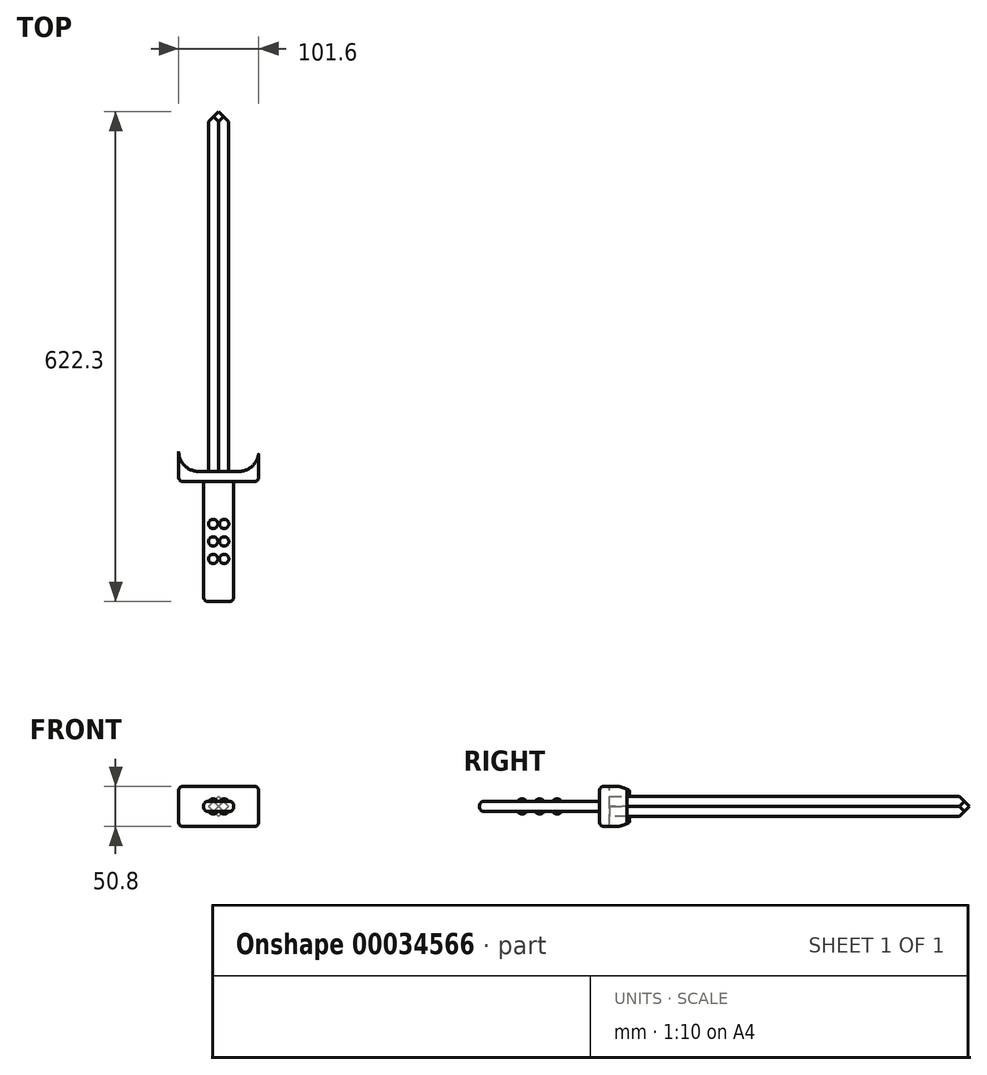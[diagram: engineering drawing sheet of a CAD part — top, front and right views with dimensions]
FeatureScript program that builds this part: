
annotation { "Feature Type Name" : "Feature", "Feature Type Description" : "" }
export const myFeature = defineFeature(function(context is Context, id is Id, definition is map)
    precondition{}
    {
        {
            var Q0;
            Q0=qCreatedBy(makeId("Front.planeOp"),FACE);
            var sketch = newSketch(context, id + "F0", { "sketchPlane" : qUnion([Q0])});
            skLineSegment(sketch, "E0.bottom", {"start": v(-20.15, -10.38) * mm, "end": v(17.95, -10.38) * mm});
            skLineSegment(sketch, "E0.top", {"start": v(-20.15, -23.08) * mm, "end": v(17.95, -23.08) * mm});
            skLineSegment(sketch, "E0.left", {"start": v(-20.15, -10.38) * mm, "end": v(-20.15, -23.08) * mm});
            skLineSegment(sketch, "E0.right", {"start": v(17.95, -10.38) * mm, "end": v(17.95, -23.08) * mm});
            skSolve(sketch);
        }
        {
            var Q0;
            Q0=makeQuery(id+"F0.imprint","IMPRINT",FACE,{"disambiguationData":[TD([[makeQuery(id+"F0.imprint","IMPRINT",EDGE,{"derivedFrom":sQuery(id+"F0.wireOp",EDGE,"E0.bottom")}),-1.0]])]});
            extrude(context, id + "F1", {"entities" : qUnion([Q0]), "oppositeDirection" : true, "depth" : 152.4 * mm});
        }
        {
            var Q0;
            Q0=makeQuery(id+"F1.opExtrude","CAP_FACE",FACE,{"disambiguationData":[OSD([sQuery(id+"F0.wireOp",EDGE,"E0.bottom"),sQuery(id+"F0.wireOp",EDGE,"E0.top"),sQuery(id+"F0.wireOp",EDGE,"E0.left"),sQuery(id+"F0.wireOp",EDGE,"E0.right")])],"isStart":false});
            var sketch = newSketch(context, id + "F2", { "sketchPlane" : qUnion([Q0])});
            skLineSegment(sketch, "E1.bottom", {"start": v(-49.7, 8.67) * mm, "end": v(51.9, 8.67) * mm});
            skLineSegment(sketch, "E1.top", {"start": v(-49.7, -42.13) * mm, "end": v(51.9, -42.13) * mm});
            skLineSegment(sketch, "E1.left", {"start": v(-49.7, 8.67) * mm, "end": v(-49.7, -42.13) * mm});
            skLineSegment(sketch, "E1.right", {"start": v(51.9, 8.67) * mm, "end": v(51.9, -42.13) * mm});
            skSolve(sketch);
        }
        {
            var Q0;
            Q0=makeQuery(id+"F2.imprint","IMPRINT",FACE,{"disambiguationData":[TD([[makeQuery(id+"F2.imprint","IMPRINT",EDGE,{"derivedFrom":sQuery(id+"F2.wireOp",EDGE,"E1.bottom")}),-1.0]])]});
            var Q1;
            Q1=makeQuery(id+"F2.imprint","IMPRINT",FACE,{"disambiguationData":[TD([[makeQuery(id+"F2.imprint","IMPRINT",EDGE,{"derivedFrom":makeQuery(id+"F1.opExtrude","CAP_EDGE",EDGE,{"disambiguationData":[OSD([sQuery(id+"F0.wireOp",EDGE,"E0.bottom")])],"isStart":false})}),1.0]])]});
            extrude(context, id + "F3", {"entities" : qUnion([Q0, Q1]), "operationType" : NewBodyOperationType.ADD, "depth" : 12.7 * mm});
        }
        {
            var Q0;
            Q0=makeQuery(id+"F3.opExtrude","CAP_EDGE",EDGE,{"disambiguationData":[OSD([sQuery(id+"F2.wireOp",EDGE,"E1.bottom")])],"isStart":true});
            var Q1;
            Q1=makeQuery(id+"F1.opExtrude","CAP_EDGE",EDGE,{"disambiguationData":[OSD([sQuery(id+"F0.wireOp",EDGE,"E0.right")])],"isStart":false});
            var Q2;
            Q2=makeQuery(id+"F1.opExtrude","CAP_EDGE",EDGE,{"disambiguationData":[OSD([sQuery(id+"F0.wireOp",EDGE,"E0.bottom")])],"isStart":false});
            var Q3;
            Q3=makeQuery(id+"F1.opExtrude","CAP_EDGE",EDGE,{"disambiguationData":[OSD([sQuery(id+"F0.wireOp",EDGE,"E0.left")])],"isStart":false});
            var Q4;
            Q4=makeQuery(id+"F1.opExtrude","CAP_EDGE",EDGE,{"disambiguationData":[OSD([sQuery(id+"F0.wireOp",EDGE,"E0.top")])],"isStart":false});
            var Q5;
            Q5=makeQuery(id+"F3.opExtrude","CAP_EDGE",EDGE,{"disambiguationData":[OSD([sQuery(id+"F2.wireOp",EDGE,"E1.left")])],"isStart":true});
            var Q6;
            Q6=makeQuery(id+"F3.opExtrude","CAP_EDGE",EDGE,{"disambiguationData":[OSD([sQuery(id+"F2.wireOp",EDGE,"E1.top")])],"isStart":true});
            var Q7;
            Q7=makeQuery(id+"F3.opExtrude","CAP_EDGE",EDGE,{"disambiguationData":[OSD([sQuery(id+"F2.wireOp",EDGE,"E1.right")])],"isStart":true});
            var Q8;
            Q8=makeQuery(id+"F1.opExtrude","SWEPT_EDGE",EDGE,{"disambiguationData":[OSD([sQuery(id+"F0.wireOp",EDGE,"E0.bottom"),sQuery(id+"F0.wireOp",EDGE,"E0.right")])]});
            var Q9;
            Q9=makeQuery(id+"F1.opExtrude","SWEPT_EDGE",EDGE,{"disambiguationData":[OSD([sQuery(id+"F0.wireOp",EDGE,"E0.top"),sQuery(id+"F0.wireOp",EDGE,"E0.right")])]});
            var Q10;
            Q10=makeQuery(id+"F1.opExtrude","CAP_EDGE",EDGE,{"disambiguationData":[OSD([sQuery(id+"F0.wireOp",EDGE,"E0.top")])],"isStart":true});
            var Q11;
            Q11=makeQuery(id+"F1.opExtrude","CAP_EDGE",EDGE,{"disambiguationData":[OSD([sQuery(id+"F0.wireOp",EDGE,"E0.bottom")])],"isStart":true});
            var Q12;
            Q12=makeQuery(id+"F1.opExtrude","SWEPT_EDGE",EDGE,{"disambiguationData":[OSD([sQuery(id+"F0.wireOp",EDGE,"E0.bottom"),sQuery(id+"F0.wireOp",EDGE,"E0.left")])]});
            var Q13;
            Q13=makeQuery(id+"F1.opExtrude","SWEPT_EDGE",EDGE,{"disambiguationData":[OSD([sQuery(id+"F0.wireOp",EDGE,"E0.top"),sQuery(id+"F0.wireOp",EDGE,"E0.left")])]});
            var Q14;
            Q14=makeQuery(id+"F1.opExtrude","CAP_EDGE",EDGE,{"disambiguationData":[OSD([sQuery(id+"F0.wireOp",EDGE,"E0.left")])],"isStart":true});
            var Q15;
            Q15=makeQuery(id+"F1.opExtrude","CAP_EDGE",EDGE,{"disambiguationData":[OSD([sQuery(id+"F0.wireOp",EDGE,"E0.right")])],"isStart":true});
            fillet(context, id + "F4", {"entities" : qUnion([Q0, Q1, Q2, Q3, Q4, Q5, Q6, Q7, Q8, Q9, Q10, Q11, Q12, Q13, Q14, Q15]), "radius" : 5.08 * mm, "tangentPropagation" : true, "allowEdgeOverflow" : false});
        }
        {
            var Q0;
            Q0=makeQuery(id+"F3.opExtrude","SWEPT_FACE",FACE,{"disambiguationData":[OSD([sQuery(id+"F2.wireOp",EDGE,"E1.bottom")])]});
            var sketch = newSketch(context, id + "F5", { "sketchPlane" : qUnion([Q0])});
            skLineSegment(sketch, "E2.bottom", {"start": v(-51.9, 165.1) * mm, "end": v(49.7, 165.1) * mm});
            skLineSegment(sketch, "E2.left", {"start": v(-51.9, 165.1) * mm, "end": v(-51.9, 190.5) * mm});
            skLineSegment(sketch, "E2.right", {"start": v(49.7, 165.1) * mm, "end": v(49.7, 190.5) * mm});
            skLineSegment(sketch, "E3.bottom", {"start": v(-51.9, 165.1) * mm, "end": v(-26.5, 165.1) * mm});
            skLineSegment(sketch, "E4.bottom", {"start": v(49.7, 165.1) * mm, "end": v(24.3, 165.1) * mm});
            skArc(sketch, "E5", {"start": v(-51.9, 190.5) * mm, "mid": v(-44.46, 172.54) * mm, "end": v(-26.5, 165.1) * mm});
            skArc(sketch, "E6", {"start": v(24.3, 165.1) * mm, "mid": v(42.26, 172.54) * mm, "end": v(49.7, 190.5) * mm});
            skSolve(sketch);
        }
        {
            var Q0;
            Q0 = qSketchRegion(id + "F5", true);
            extrude(context, id + "F6", {"entities" : qUnion([Q0]), "operationType" : NewBodyOperationType.ADD, "oppositeDirection" : true, "depth" : 50.8 * mm});
        }
        {
            var Q0;
            Q0=makeQuery(id+"F6.boolean.opBoolean","MERGE",EDGE,{"derivedFrom":[makeQuery(id+"F3.opExtrude","SWEPT_EDGE",EDGE,{"disambiguationData":[OSD([sQuery(id+"F2.wireOp",EDGE,"E1.bottom"),sQuery(id+"F2.wireOp",EDGE,"E1.left")])]}),makeQuery(id+"F6.opExtrude","CAP_EDGE",EDGE,{"disambiguationData":[OSD([sQuery(id+"F5.wireOp",EDGE,"92b06a6b-4f89-4f7e-b0d3-59be5738ee68.left")])],"isStart":true})]});
            var Q1;
            Q1=makeQuery(id+"F6.opExtrude","CAP_EDGE",EDGE,{"disambiguationData":[OSD([sQuery(id+"F5.wireOp",EDGE,"0fc54be1-5544-46dc-9fd6-cf08e8844ddd")])],"isStart":true});
            var Q2;
            Q2=makeQuery(id+"F6.opExtrude","CAP_EDGE",EDGE,{"disambiguationData":[OSD([sQuery(id+"F5.wireOp",EDGE,"522da2e3-5dac-4369-9592-a29fee154710.trimOffspring")])],"isStart":false});
            var Q3;
            Q3=makeQuery(id+"F6.boolean.opBoolean","MERGE",EDGE,{"derivedFrom":[makeQuery(id+"F3.opExtrude","SWEPT_EDGE",EDGE,{"disambiguationData":[OSD([sQuery(id+"F2.wireOp",EDGE,"E1.top"),sQuery(id+"F2.wireOp",EDGE,"E1.left")])]}),makeQuery(id+"F6.opExtrude","CAP_EDGE",EDGE,{"disambiguationData":[OSD([sQuery(id+"F5.wireOp",EDGE,"92b06a6b-4f89-4f7e-b0d3-59be5738ee68.left")])],"isStart":false})]});
            var Q4;
            Q4=makeQuery(id+"F6.boolean.opBoolean","MERGE",EDGE,{"derivedFrom":[makeQuery(id+"F3.opExtrude","SWEPT_EDGE",EDGE,{"disambiguationData":[OSD([sQuery(id+"F2.wireOp",EDGE,"E1.bottom"),sQuery(id+"F2.wireOp",EDGE,"E1.right")])]}),makeQuery(id+"F6.opExtrude","CAP_EDGE",EDGE,{"disambiguationData":[OSD([sQuery(id+"F5.wireOp",EDGE,"92b06a6b-4f89-4f7e-b0d3-59be5738ee68.right")])],"isStart":true})]});
            var Q5;
            Q5=makeQuery(id+"F6.boolean.opBoolean","MERGE",EDGE,{"derivedFrom":[makeQuery(id+"F3.opExtrude","SWEPT_EDGE",EDGE,{"disambiguationData":[OSD([sQuery(id+"F2.wireOp",EDGE,"E1.top"),sQuery(id+"F2.wireOp",EDGE,"E1.right")])]}),makeQuery(id+"F6.opExtrude","CAP_EDGE",EDGE,{"disambiguationData":[OSD([sQuery(id+"F5.wireOp",EDGE,"92b06a6b-4f89-4f7e-b0d3-59be5738ee68.right")])],"isStart":false})]});
            fillet(context, id + "F7", {"entities" : qUnion([Q0, Q1, Q2, Q3, Q4, Q5]), "radius" : 5.08 * mm, "tangentPropagation" : true, "allowEdgeOverflow" : false});
        }
        {
            var Q0;
            Q0=makeQuery(id+"F3.opExtrude","CAP_FACE",FACE,{"disambiguationData":[OSD([sQuery(id+"F2.wireOp",EDGE,"E1.bottom"),sQuery(id+"F2.wireOp",EDGE,"E1.top"),sQuery(id+"F2.wireOp",EDGE,"E1.left"),sQuery(id+"F2.wireOp",EDGE,"E1.right")])],"isStart":false});
            var sketch = newSketch(context, id + "F8", { "sketchPlane" : qUnion([Q0])});
            skLineSegment(sketch, "E7.bottom", {"start": v(-11.6, -4.03) * mm, "end": v(13.8, -4.03) * mm});
            skLineSegment(sketch, "E7.top", {"start": v(-11.6, -29.43) * mm, "end": v(13.8, -29.43) * mm});
            skLineSegment(sketch, "E7.left", {"start": v(-11.6, -4.03) * mm, "end": v(-11.6, -29.43) * mm});
            skLineSegment(sketch, "E7.right", {"start": v(13.8, -4.03) * mm, "end": v(13.8, -29.43) * mm});
            skSolve(sketch);
        }
        {
            var Q0;
            Q0 = qSketchRegion(id + "F8", true);
            extrude(context, id + "F9", {"entities" : qUnion([Q0]), "operationType" : NewBodyOperationType.ADD, "depth" : 457.2 * mm});
        }
        {
            var Q0;
            Q0=makeQuery(id+"F6.opExtrude","SWEPT_EDGE",EDGE,{"disambiguationData":[OSD([sQuery(id+"F5.wireOp",EDGE,"E2.right"),sQuery(id+"F5.wireOp",EDGE,"E6")])]});
            fillet(context, id + "F10", {"entities" : qUnion([Q0]), "radius" : 0.13 * mm, "tangentPropagation" : true, "allowEdgeOverflow" : false});
        }
        {
            var Q0;
            Q0=makeQuery(id+"F9.opExtrude","CAP_EDGE",EDGE,{"disambiguationData":[OSD([sQuery(id+"F8.wireOp",EDGE,"E7.bottom")])],"isStart":false});
            var Q1;
            Q1=makeQuery(id+"F9.opExtrude","CAP_EDGE",EDGE,{"disambiguationData":[OSD([sQuery(id+"F8.wireOp",EDGE,"E7.top")])],"isStart":false});
            var Q2;
            Q2=makeQuery(id+"F9.opExtrude","CAP_EDGE",EDGE,{"disambiguationData":[OSD([sQuery(id+"F8.wireOp",EDGE,"E7.left")])],"isStart":false});
            var Q3;
            Q3=makeQuery(id+"F9.opExtrude","CAP_EDGE",EDGE,{"disambiguationData":[OSD([sQuery(id+"F8.wireOp",EDGE,"E7.right")])],"isStart":false});
            chamfer(context, id + "F11", {"entities" : qUnion([Q0, Q1, Q2, Q3]), "width" : 12.7 * mm, "tangentPropagation" : true});
        }
        {
            var Q0;
            Q0=makeQuery(id+"F9.opExtrude","SWEPT_EDGE",EDGE,{"disambiguationData":[OSD([sQuery(id+"F5.wireOp",EDGE,"92b06a6b-4f89-4f7e-b0d3-59be5738ee68.bottom"),sQuery(id+"F5.wireOp",EDGE,"0fc54be1-5544-46dc-9fd6-cf08e8844ddd"),sQuery(id+"F8.wireOp",EDGE,"E7.top"),sQuery(id+"F8.wireOp",EDGE,"E7.left")])]});
            var Q1;
            Q1=makeQuery(id+"F9.opExtrude","SWEPT_EDGE",EDGE,{"disambiguationData":[OSD([sQuery(id+"F5.wireOp",EDGE,"92b06a6b-4f89-4f7e-b0d3-59be5738ee68.bottom"),sQuery(id+"F5.wireOp",EDGE,"522da2e3-5dac-4369-9592-a29fee154710.trimOffspring"),sQuery(id+"F8.wireOp",EDGE,"E7.top"),sQuery(id+"F8.wireOp",EDGE,"E7.right")])]});
            var Q2;
            Q2=makeQuery(id+"F9.opExtrude","SWEPT_EDGE",EDGE,{"disambiguationData":[OSD([sQuery(id+"F5.wireOp",EDGE,"92b06a6b-4f89-4f7e-b0d3-59be5738ee68.bottom"),sQuery(id+"F5.wireOp",EDGE,"0fc54be1-5544-46dc-9fd6-cf08e8844ddd"),sQuery(id+"F8.wireOp",EDGE,"E7.bottom"),sQuery(id+"F8.wireOp",EDGE,"E7.left")])]});
            var Q3;
            Q3=makeQuery(id+"F9.opExtrude","SWEPT_EDGE",EDGE,{"disambiguationData":[OSD([sQuery(id+"F5.wireOp",EDGE,"92b06a6b-4f89-4f7e-b0d3-59be5738ee68.bottom"),sQuery(id+"F5.wireOp",EDGE,"522da2e3-5dac-4369-9592-a29fee154710.trimOffspring"),sQuery(id+"F8.wireOp",EDGE,"E7.bottom"),sQuery(id+"F8.wireOp",EDGE,"E7.right")])]});
            chamfer(context, id + "F12", {"entities" : qUnion([Q0, Q1, Q2, Q3]), "width" : 12.7 * mm, "tangentPropagation" : true});
        }
        {
            var Q0;
            Q0=makeQuery(id+"F1.opExtrude","SWEPT_FACE",FACE,{"disambiguationData":[OSD([sQuery(id+"F0.wireOp",EDGE,"E0.bottom")])]});
            var sketch = newSketch(context, id + "F13", { "sketchPlane" : qUnion([Q0])});
            skCircle(sketch, "E8", {"center": v(-8.09, 98.43) * mm, "radius": 5.91 * mm});
            skCircle(sketch, "E9", {"center": v(5.88, 98.43) * mm, "radius": 5.91 * mm});
            skCircle(sketch, "E10", {"center": v(-8.09, 76.2) * mm, "radius": 5.91 * mm});
            skCircle(sketch, "E11", {"center": v(5.88, 76.2) * mm, "radius": 5.91 * mm});
            skCircle(sketch, "E12", {"center": v(-8.09, 53.97) * mm, "radius": 5.91 * mm});
            skCircle(sketch, "E13", {"center": v(5.88, 53.97) * mm, "radius": 5.91 * mm});
            skLineSegment(sketch, "E14", {"start": v(-8.09, 98.43) * mm, "end": v(-8.09, 76.2) * mm});
            skLineSegment(sketch, "E15", {"start": v(-8.09, 76.2) * mm, "end": v(-8.09, 53.97) * mm});
            skLineSegment(sketch, "E16", {"start": v(5.88, 98.43) * mm, "end": v(5.88, 76.2) * mm});
            skLineSegment(sketch, "E17", {"start": v(5.88, 76.2) * mm, "end": v(5.88, 53.97) * mm});
            skLineSegment(sketch, "E18", {"start": v(-8.09, 87.31) * mm, "end": v(-15.07, 87.31) * mm});
            skLineSegment(sketch, "E19", {"start": v(5.88, 87.31) * mm, "end": v(12.87, 87.31) * mm});
            skLineSegment(sketch, "E20", {"start": v(-8.09, 98.43) * mm, "end": v(-8.09, 147.32) * mm});
            skLineSegment(sketch, "E21", {"start": v(5.88, 98.43) * mm, "end": v(5.88, 147.32) * mm});
            skPoint(sketch, "E22", {"position": v(-15.07, 65.52) * mm});
            skPoint(sketch, "E23", {"position": v(12.87, 65.52) * mm});
            skLineSegment(sketch, "E24", {"start": v(5.88, 53.97) * mm, "end": v(5.88, 5.08) * mm});
            skLineSegment(sketch, "E25", {"start": v(-8.09, 53.97) * mm, "end": v(-8.09, 5.08) * mm});
            skSolve(sketch);
        }
        {
            var Q0;
            Q0 = qSketchRegion(id + "F13", true);
            extrude(context, id + "F14", {"entities" : qUnion([Q0]), "operationType" : NewBodyOperationType.ADD, "depth" : 3.17 * mm});
        }
        {
            var Q0;
            Q0=makeQuery(id+"F14.opExtrude","CAP_EDGE",EDGE,{"disambiguationData":[OSD([sQuery(id+"F13.wireOp",EDGE,"E13")])],"isStart":false});
            var Q1;
            Q1=makeQuery(id+"F14.opExtrude","CAP_FACE",FACE,{"disambiguationData":[OSD([sQuery(id+"F13.wireOp",EDGE,"E12")])],"isStart":false});
            var Q2;
            Q2=makeQuery(id+"F14.opExtrude","CAP_EDGE",EDGE,{"disambiguationData":[OSD([sQuery(id+"F13.wireOp",EDGE,"E11")])],"isStart":false});
            var Q3;
            Q3=makeQuery(id+"F14.opExtrude","CAP_EDGE",EDGE,{"disambiguationData":[OSD([sQuery(id+"F13.wireOp",EDGE,"E10")])],"isStart":false});
            var Q4;
            Q4=makeQuery(id+"F14.opExtrude","CAP_EDGE",EDGE,{"disambiguationData":[OSD([sQuery(id+"F13.wireOp",EDGE,"E9")])],"isStart":false});
            var Q5;
            Q5=makeQuery(id+"F14.opExtrude","CAP_EDGE",EDGE,{"disambiguationData":[OSD([sQuery(id+"F13.wireOp",EDGE,"E8")])],"isStart":false});
            var Q6;
            Q6=makeQuery(id+"F14.opExtrude","CAP_FACE",FACE,{"disambiguationData":[OSD([sQuery(id+"F13.wireOp",EDGE,"E11")])],"isStart":false});
            fillet(context, id + "F15", {"entities" : qUnion([Q0, Q1, Q2, Q3, Q4, Q5, Q6]), "radius" : 7.08 * mm, "tangentPropagation" : true, "allowEdgeOverflow" : false});
        }
        {
            var Q0;
            Q0=makeQuery(id+"F1.opExtrude","SWEPT_FACE",FACE,{"disambiguationData":[OSD([sQuery(id+"F0.wireOp",EDGE,"E0.top")])]});
            var sketch = newSketch(context, id + "F16", { "sketchPlane" : qUnion([Q0])});
            skCircle(sketch, "E26", {"center": v(-8.09, -53.97) * mm, "radius": 5.91 * mm});
            skCircle(sketch, "E27", {"center": v(5.88, -53.97) * mm, "radius": 5.91 * mm});
            skCircle(sketch, "E28", {"center": v(-8.09, -76.2) * mm, "radius": 5.91 * mm});
            skCircle(sketch, "E29", {"center": v(5.88, -76.2) * mm, "radius": 5.91 * mm});
            skCircle(sketch, "E30", {"center": v(-8.09, -98.42) * mm, "radius": 5.91 * mm});
            skCircle(sketch, "E31", {"center": v(5.88, -98.43) * mm, "radius": 5.91 * mm});
            skLineSegment(sketch, "E32", {"start": v(-8.09, -53.97) * mm, "end": v(-8.09, -76.2) * mm});
            skLineSegment(sketch, "E33", {"start": v(-8.09, -76.2) * mm, "end": v(-8.09, -98.42) * mm});
            skLineSegment(sketch, "E34", {"start": v(5.88, -53.97) * mm, "end": v(5.88, -76.2) * mm});
            skLineSegment(sketch, "E35", {"start": v(5.88, -76.2) * mm, "end": v(5.88, -98.43) * mm});
            skLineSegment(sketch, "E36", {"start": v(-8.09, -53.97) * mm, "end": v(-8.09, -5.08) * mm});
            skLineSegment(sketch, "E37", {"start": v(5.88, -53.97) * mm, "end": v(5.88, -5.08) * mm});
            skLineSegment(sketch, "E38", {"start": v(5.88, -98.43) * mm, "end": v(5.88, -147.32) * mm});
            skLineSegment(sketch, "E39", {"start": v(-8.09, -98.42) * mm, "end": v(-8.09, -147.32) * mm});
            skLineSegment(sketch, "E40", {"start": v(-8.09, -76.2) * mm, "end": v(-15.07, -76.2) * mm});
            skLineSegment(sketch, "E41", {"start": v(5.88, -76.2) * mm, "end": v(12.87, -76.2) * mm});
            skSolve(sketch);
        }
        {
            var Q0;
            Q0 = qSketchRegion(id + "F16", true);
            extrude(context, id + "F17", {"entities" : qUnion([Q0]), "operationType" : NewBodyOperationType.ADD, "depth" : 3.17 * mm});
        }
        {
            var Q0;
            Q0=makeQuery(id+"F17.opExtrude","CAP_EDGE",EDGE,{"disambiguationData":[OSD([sQuery(id+"F16.wireOp",EDGE,"E26")])],"isStart":false});
            var Q1;
            Q1=makeQuery(id+"F17.opExtrude","CAP_EDGE",EDGE,{"disambiguationData":[OSD([sQuery(id+"F16.wireOp",EDGE,"E27")])],"isStart":false});
            var Q2;
            Q2=makeQuery(id+"F17.opExtrude","CAP_EDGE",EDGE,{"disambiguationData":[OSD([sQuery(id+"F16.wireOp",EDGE,"E28")])],"isStart":false});
            var Q3;
            Q3=makeQuery(id+"F17.opExtrude","CAP_EDGE",EDGE,{"disambiguationData":[OSD([sQuery(id+"F16.wireOp",EDGE,"E29")])],"isStart":false});
            var Q4;
            Q4=makeQuery(id+"F17.opExtrude","CAP_EDGE",EDGE,{"disambiguationData":[OSD([sQuery(id+"F16.wireOp",EDGE,"E30")])],"isStart":false});
            var Q5;
            Q5=makeQuery(id+"F17.opExtrude","CAP_EDGE",EDGE,{"disambiguationData":[OSD([sQuery(id+"F16.wireOp",EDGE,"E31")])],"isStart":false});
            fillet(context, id + "F18", {"entities" : qUnion([Q0, Q1, Q2, Q3, Q4, Q5]), "radius" : 7.08 * mm, "tangentPropagation" : true, "allowEdgeOverflow" : false});
        }
    });
